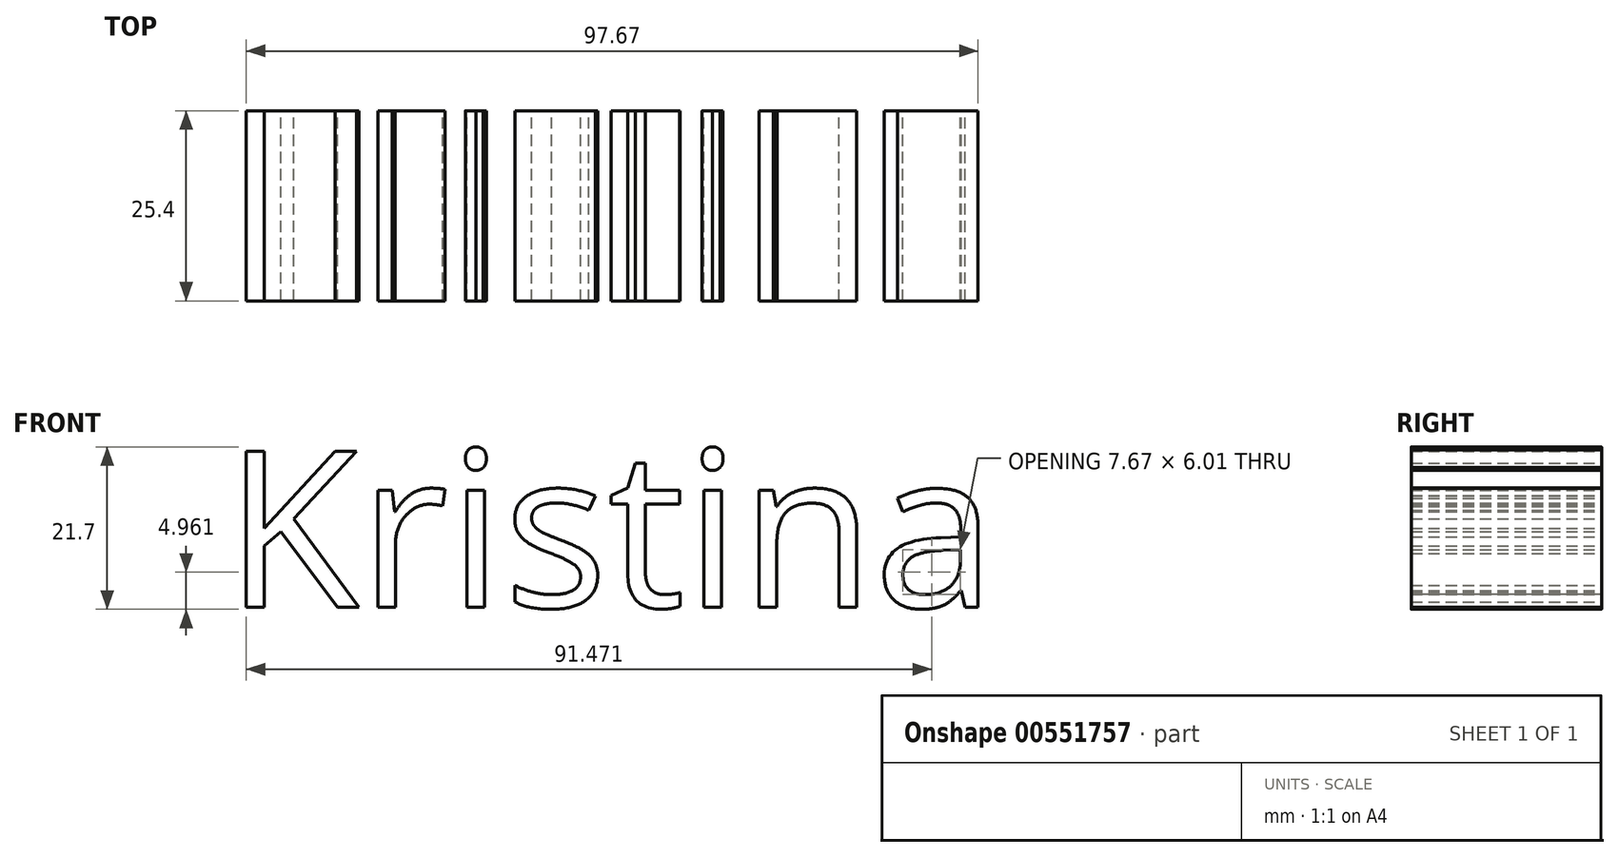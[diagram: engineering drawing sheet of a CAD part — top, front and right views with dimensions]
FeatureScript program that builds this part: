
annotation { "Feature Type Name" : "Feature", "Feature Type Description" : "" }
export const myFeature = defineFeature(function(context is Context, id is Id, definition is map)
    precondition{}
    {
        {
            var Q0;
            Q0=qCreatedBy(makeId("Front.planeOp"),FACE);
            var sketch = newSketch(context, id + "F0", { "sketchPlane" : qUnion([Q0])});
            skText(sketch, "E0", { "text": "Kristina ", "fontName": "OpenSans-Regular.ttf"});
            const initialGuessF0  = {"E0": [-0.04963, 0.00898, 1, 0, 0.021]};
            skSetInitialGuess(sketch, initialGuessF0);
            skSolve(sketch);
        }
        {
            var Q0;
            Q0=makeQuery(id+"F0.imprint","IMPRINT",FACE,{"disambiguationData":[TD([[makeQuery(id+"F0.imprint","IMPRINT",EDGE,{"derivedFrom":sQuery(id+"F0.wireOp",EDGE,"E0.sketch_text.stroke-0")}),-1.0]])]});
            var Q1;
            Q1=makeQuery(id+"F0.imprint","IMPRINT",FACE,{"disambiguationData":[TD([[makeQuery(id+"F0.imprint","IMPRINT",EDGE,{"derivedFrom":sQuery(id+"F0.wireOp",EDGE,"E0.sketch_text.stroke-12")}),-1.0]])]});
            var Q2;
            Q2=makeQuery(id+"F0.imprint","IMPRINT",FACE,{"disambiguationData":[TD([[makeQuery(id+"F0.imprint","IMPRINT",EDGE,{"derivedFrom":sQuery(id+"F0.wireOp",EDGE,"E0.sketch_text.stroke-25")}),-1.0]])]});
            var Q3;
            Q3=makeQuery(id+"F0.imprint","IMPRINT",FACE,{"disambiguationData":[TD([[makeQuery(id+"F0.imprint","IMPRINT",EDGE,{"derivedFrom":sQuery(id+"F0.wireOp",EDGE,"E0.sketch_text.stroke-29")}),-1.0]])]});
            var Q4;
            Q4=makeQuery(id+"F0.imprint","IMPRINT",FACE,{"disambiguationData":[TD([[makeQuery(id+"F0.imprint","IMPRINT",EDGE,{"derivedFrom":sQuery(id+"F0.wireOp",EDGE,"E0.sketch_text.stroke-37")}),-1.0]])]});
            var Q5;
            Q5=makeQuery(id+"F0.imprint","IMPRINT",FACE,{"disambiguationData":[TD([[makeQuery(id+"F0.imprint","IMPRINT",EDGE,{"derivedFrom":sQuery(id+"F0.wireOp",EDGE,"E0.sketch_text.stroke-62")}),-1.0]])]});
            var Q6;
            Q6=makeQuery(id+"F0.imprint","IMPRINT",FACE,{"disambiguationData":[TD([[makeQuery(id+"F0.imprint","IMPRINT",EDGE,{"derivedFrom":sQuery(id+"F0.wireOp",EDGE,"E0.sketch_text.stroke-85")}),-1.0]])]});
            var Q7;
            Q7=makeQuery(id+"F0.imprint","IMPRINT",FACE,{"disambiguationData":[TD([[makeQuery(id+"F0.imprint","IMPRINT",EDGE,{"derivedFrom":sQuery(id+"F0.wireOp",EDGE,"E0.sketch_text.stroke-81")}),-1.0]])]});
            var Q8;
            Q8=makeQuery(id+"F0.imprint","IMPRINT",FACE,{"disambiguationData":[TD([[makeQuery(id+"F0.imprint","IMPRINT",EDGE,{"derivedFrom":sQuery(id+"F0.wireOp",EDGE,"E0.sketch_text.stroke-93")}),-1.0]])]});
            var Q9;
            Q9=makeQuery(id+"F0.imprint","IMPRINT",FACE,{"disambiguationData":[TD([[makeQuery(id+"F0.imprint","IMPRINT",EDGE,{"derivedFrom":sQuery(id+"F0.wireOp",EDGE,"E0.sketch_text.stroke-110")}),-1.0]])]});
            extrude(context, id + "F1", {"entities" : qUnion([Q0, Q1, Q2, Q3, Q4, Q5, Q6, Q7, Q8, Q9]), "depth" : 25.4 * mm, "offsetDistance" : 25.4 * mm});
        }
    });
